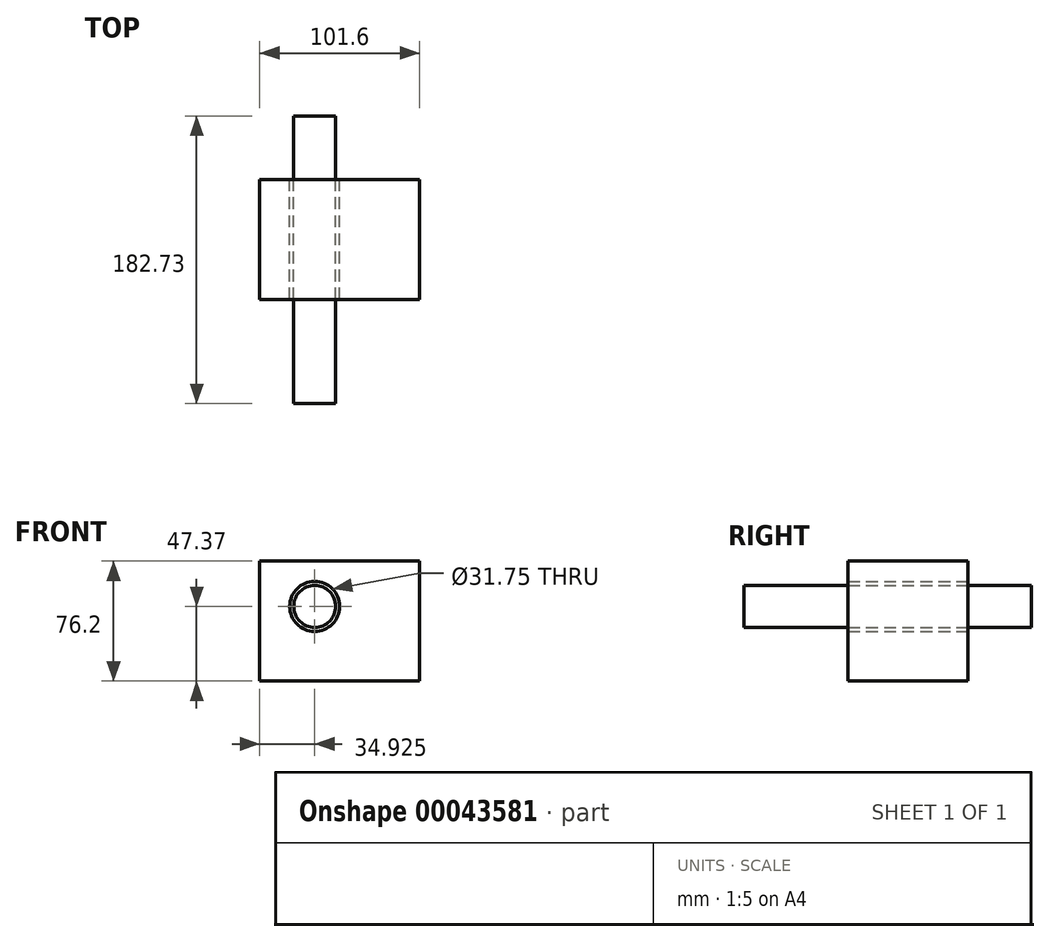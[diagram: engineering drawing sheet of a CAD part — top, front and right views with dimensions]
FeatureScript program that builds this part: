
annotation { "Feature Type Name" : "Feature", "Feature Type Description" : "" }
export const myFeature = defineFeature(function(context is Context, id is Id, definition is map)
    precondition{}
    {
        {
            var Q0;
            Q0=qCreatedBy(makeId("Front.planeOp"),FACE);
            var sketch = newSketch(context, id + "F0", { "sketchPlane" : qUnion([Q0])});
            skLineSegment(sketch, "E0.bottom", {"start": v(0, 0) * mm, "end": v(101.6, 0) * mm});
            skLineSegment(sketch, "E0.top", {"start": v(0, 76.2) * mm, "end": v(101.6, 76.2) * mm});
            skLineSegment(sketch, "E0.left", {"start": v(0, 0) * mm, "end": v(0, 76.2) * mm});
            skLineSegment(sketch, "E0.right", {"start": v(101.6, 0) * mm, "end": v(101.6, 76.2) * mm});
            skCircle(sketch, "E1", {"center": v(34.92, 47.37) * mm, "radius": 15.88 * mm});
            skSolve(sketch);
        }
        {
            var Q0;
            Q0 = qSketchRegion(id + "F0", true);
            extrude(context, id + "F1", {"entities" : qUnion([Q0]), "depth" : 76.2 * mm});
        }
        {
            var Q0;
            Q0=makeQuery(id+"F1.opExtrude","CAP_FACE",FACE,{"disambiguationData":[OSD([sQuery(id+"F0.wireOp",EDGE,"E0.bottom"),sQuery(id+"F0.wireOp",EDGE,"E0.top"),sQuery(id+"F0.wireOp",EDGE,"E0.left"),sQuery(id+"F0.wireOp",EDGE,"E0.right"),sQuery(id+"F0.wireOp",EDGE,"E1")])],"isStart":false});
            var sketch = newSketch(context, id + "F2", { "sketchPlane" : qUnion([Q0])});
            skCircle(sketch, "E2.0", {"center": v(34.92, 47.37) * mm, "radius": 13.33 * mm});
            skSolve(sketch);
        }
        {
            var Q0;
            Q0 = qSketchRegion(id + "F2", true);
            extrude(context, id + "F3", {"entities" : qUnion([Q0]), "depth" : 66.1 * mm, "hasSecondDirection" : true, "secondDirectionOppositeDirection" : true, "secondDirectionDepth" : 116.63 * mm});
        }
    });
